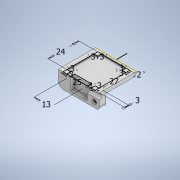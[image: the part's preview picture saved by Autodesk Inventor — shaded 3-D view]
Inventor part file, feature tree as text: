
AUTODESK INVENTOR PART (.ipt)
format: ipt  version: 2020.3 (Build 243373000, 373)  size: 247,808 bytes
history: native  units: mm
features: extrude x9, sketch x8, fillet x2, mirror x1
ambient origin geometry x8: Origin, YZ Plane, XZ Plane, XY Plane, X Axis, Y Axis, Z Axis, Center Point
bodies: Volumenkörper1 (feature_tree)
feature tree (20):
  extrude  "Extrusion1"  Depth=11.6mm
  mirror  "Spiegeln1"
  extrude  "Extrusion2"  Depth=4.2mm
  extrude  "Extrusion3"  Depth=16.0mm
  sketch  "Skizze4"  dims[d6=24.0mm d7=0.0mm d8=12.0mm]
  extrude  "Extrusion4"  Depth=12.0mm
  extrude  "Extrusion5"  Depth=5.0mm
  extrude  "Extrusion6"  Depth=0.3mm
  extrude  "Extrusion7"  Depth=25.0mm
  extrude  "Extrusion8"  Depth=2.0mm
  extrude  "Extrusion10"  Depth=20.5mm
  fillet  "Rundung1"  Radius=3.0mm
  fillet  "Rundung2"  Radius=13.0mm
  sketch  "Skizze1"  dims[d0=9.6mm d1=11.6mm]
  sketch  "Skizze2"  dims[d2=1.6mm d3=4.2mm]
  sketch  "Skizze3"  dims[d4=7.0mm d5=16.0mm]
  sketch  "Skizze5"  dims[d9=5.0mm d10=0.0mm d12=8.0mm]
  sketch  "Skizze6"  dims[d13=1.7mm d14=0.3mm]
  sketch  "Skizze7"  dims[d15=14.0mm d16=0.0mm d17=25.0mm]
  sketch  "Skizze9"  dims[d18=27.0mm d19=2.0mm d20=20.5mm d21=3.0mm d22=13.0mm d23=24.0mm d24=3.0mm d25=3.0mm d26=3.0mm d27=3.0mm d28=3.0mm d29=3.0mm d30=3.0mm d31=3.0mm d32=1.0mm d33=0.0mm d34=10.0mm d35=0.0mm d36=3.5mm d37=4.0mm d38=4.0mm d39=6.75mm d40=0.0mm d42=5.9mm d43=7.5mm d44=0.0mm d45=4.0mm d46=3.0mm d47=10.0mm d48=0.0mm d58=10.0mm d59=0.0mm d60=1.0mm d61=1.2mm d62=0.2mm d63=2.5mm d64=4.0mm d65=1.3mm]
